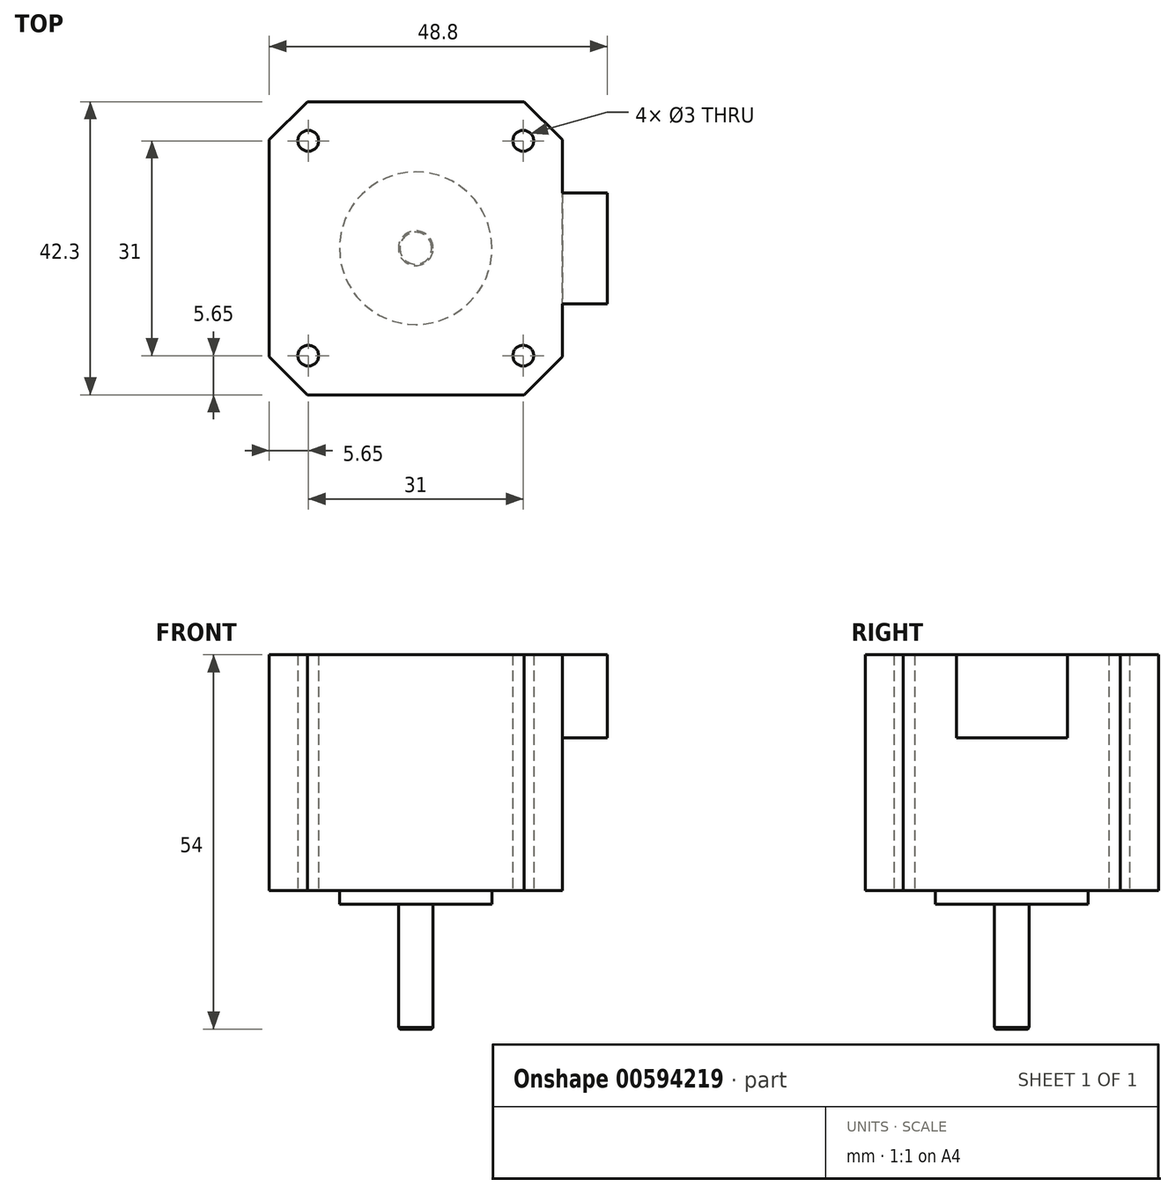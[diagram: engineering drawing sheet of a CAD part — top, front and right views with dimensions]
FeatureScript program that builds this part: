
annotation { "Feature Type Name" : "Feature", "Feature Type Description" : "" }
export const myFeature = defineFeature(function(context is Context, id is Id, definition is map)
    precondition{}
    {
        {
            var Q0;
            Q0=qCreatedBy(makeId("Top.planeOp"),FACE);
            var sketch = newSketch(context, id + "F0", { "sketchPlane" : qUnion([Q0])});
            skCircle(sketch, "E0", {"center": v(0, 0) * mm, "radius": 11 * mm});
            skLineSegment(sketch, "E1.bottom", {"start": v(21.15, -21.15) * mm, "end": v(-21.15, -21.15) * mm});
            skLineSegment(sketch, "E1.top", {"start": v(21.15, 21.15) * mm, "end": v(-21.15, 21.15) * mm});
            skLineSegment(sketch, "E1.left", {"start": v(21.15, -21.15) * mm, "end": v(21.15, 21.15) * mm});
            skLineSegment(sketch, "E1.right", {"start": v(-21.15, -21.15) * mm, "end": v(-21.15, 21.15) * mm});
            skCircle(sketch, "E2", {"center": v(0, 0) * mm, "radius": 2.5 * mm});
            skCircle(sketch, "E3", {"center": v(-15.5, 15.5) * mm, "radius": 1.5 * mm});
            skCircle(sketch, "E4", {"center": v(15.5, 15.5) * mm, "radius": 1.5 * mm});
            skCircle(sketch, "E5", {"center": v(15.5, -15.5) * mm, "radius": 1.5 * mm});
            skCircle(sketch, "E6", {"center": v(-15.5, -15.5) * mm, "radius": 1.5 * mm});
            skSolve(sketch);
        }
        {
            var Q0;
            Q0=makeQuery(id+"F0.imprint","IMPRINT",FACE,{"disambiguationData":[TD([[makeQuery(id+"F0.imprint","IMPRINT",EDGE,{"derivedFrom":sQuery(id+"F0.wireOp",EDGE,"E0")}),-1.0]])]});
            var Q1;
            Q1=makeQuery(id+"F0.imprint","IMPRINT",FACE,{"disambiguationData":[TD([[makeQuery(id+"F0.imprint","IMPRINT",EDGE,{"derivedFrom":sQuery(id+"F0.wireOp",EDGE,"E0")}),1.0]])]});
            var Q2;
            Q2=makeQuery(id+"F0.imprint","IMPRINT",FACE,{"disambiguationData":[TD([[makeQuery(id+"F0.imprint","IMPRINT",EDGE,{"derivedFrom":sQuery(id+"F0.wireOp",EDGE,"E2")}),1.0]])]});
            extrude(context, id + "F1", {"entities" : qUnion([Q0, Q1, Q2]), "depth" : 34 * mm});
        }
        {
            var Q0;
            Q0=makeQuery(id+"F0.imprint","IMPRINT",FACE,{"disambiguationData":[TD([[makeQuery(id+"F0.imprint","IMPRINT",EDGE,{"derivedFrom":sQuery(id+"F0.wireOp",EDGE,"E0")}),1.0]])]});
            extrude(context, id + "F2", {"entities" : qUnion([Q0]), "operationType" : NewBodyOperationType.ADD, "oppositeDirection" : true, "depth" : 2 * mm});
        }
        {
            var Q0;
            Q0=makeQuery(id+"F0.imprint","IMPRINT",FACE,{"disambiguationData":[TD([[makeQuery(id+"F0.imprint","IMPRINT",EDGE,{"derivedFrom":sQuery(id+"F0.wireOp",EDGE,"E2")}),1.0]])]});
            var Q1;
            Q1=sQuery(id+"F0.wireOp",EDGE,"E2");
            extrude(context, id + "F3", {"entities" : qUnion([Q0]), "operationType" : NewBodyOperationType.ADD, "surfaceEntities" : qUnion([Q1]), "oppositeDirection" : true, "depth" : 20 * mm});
        }
        {
            var Q0;
            Q0=makeQuery(id+"F1.opExtrude","SWEPT_EDGE",EDGE,{"disambiguationData":[OSD([sQuery(id+"F0.wireOp",EDGE,"E1.bottom"),sQuery(id+"F0.wireOp",EDGE,"E1.right")])]});
            var Q1;
            Q1=makeQuery(id+"F1.opExtrude","SWEPT_EDGE",EDGE,{"disambiguationData":[OSD([sQuery(id+"F0.wireOp",EDGE,"E1.bottom"),sQuery(id+"F0.wireOp",EDGE,"E1.left")])]});
            var Q2;
            Q2=makeQuery(id+"F1.opExtrude","SWEPT_EDGE",EDGE,{"disambiguationData":[OSD([sQuery(id+"F0.wireOp",EDGE,"E1.top"),sQuery(id+"F0.wireOp",EDGE,"E1.left")])]});
            var Q3;
            Q3=makeQuery(id+"F1.opExtrude","SWEPT_EDGE",EDGE,{"disambiguationData":[OSD([sQuery(id+"F0.wireOp",EDGE,"E1.top"),sQuery(id+"F0.wireOp",EDGE,"E1.right")])]});
            chamfer(context, id + "F4", {"entities" : qUnion([Q0, Q1, Q2, Q3]), "width" : 5.5 * mm, "tangentPropagation" : true});
        }
        {
            var Q0;
            Q0=makeQuery(id+"F3.opExtrude","CAP_EDGE",EDGE,{"disambiguationData":[OSD([sQuery(id+"F0.wireOp",EDGE,"E2")])],"isStart":false});
            chamfer(context, id + "F5", {"entities" : qUnion([Q0]), "width" : .2 * mm, "tangentPropagation" : true});
        }
        {
            var Q0;
            Q0=makeQuery(id+"F1.opExtrude","SWEPT_FACE",FACE,{"disambiguationData":[OSD([sQuery(id+"F0.wireOp",EDGE,"E1.left")])]});
            var sketch = newSketch(context, id + "F6", { "sketchPlane" : qUnion([Q0])});
            skLineSegment(sketch, "E7.bottom", {"start": v(8, 34) * mm, "end": v(-8, 34) * mm});
            skLineSegment(sketch, "E7.top", {"start": v(8, 22) * mm, "end": v(-8, 22) * mm});
            skLineSegment(sketch, "E7.left", {"start": v(8, 34) * mm, "end": v(8, 22) * mm});
            skLineSegment(sketch, "E7.right", {"start": v(-8, 34) * mm, "end": v(-8, 22) * mm});
            skPoint(sketch, "E7.middle", {"position": v(0, 28) * mm});
            skSolve(sketch);
        }
        {
            var Q0;
            Q0=qSketchRegion(id+"F6",true);
            extrude(context, id + "F7", {"entities" : qUnion([Q0]), "operationType" : NewBodyOperationType.ADD, "depth" : 6.5 * mm});
        }
    });
